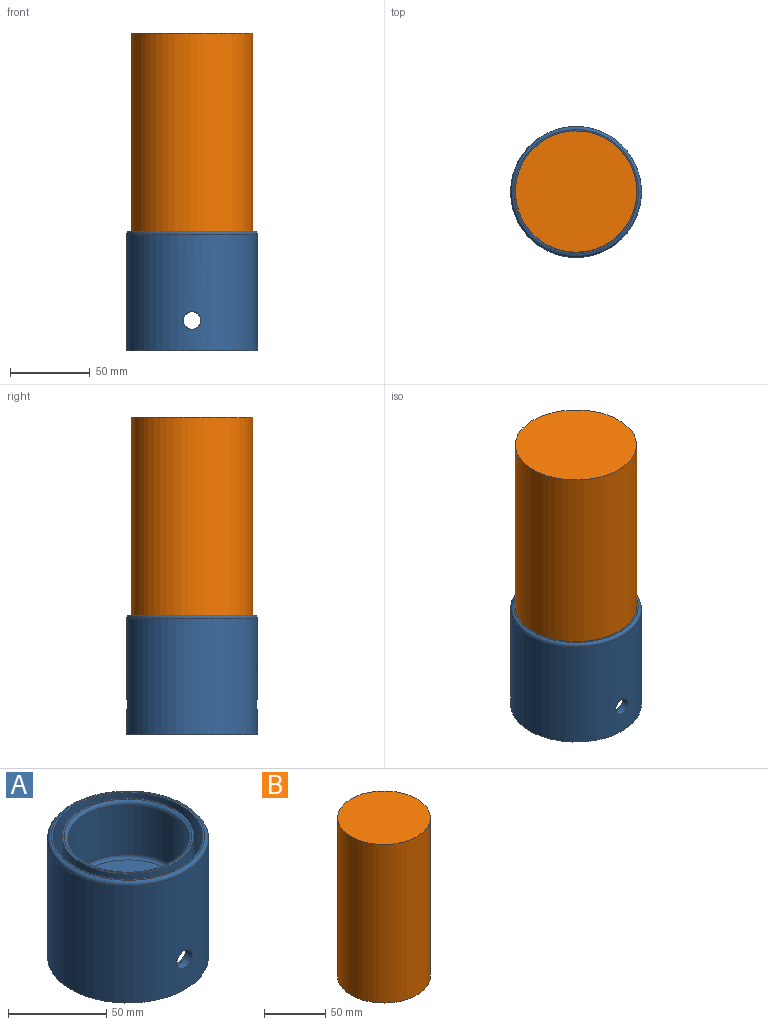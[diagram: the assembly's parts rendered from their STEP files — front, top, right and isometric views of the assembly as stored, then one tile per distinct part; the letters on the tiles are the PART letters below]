
ASSEMBLY  parts=2 mates=1
PART A: 24 faces, bbox 88.8x88.8x75 mm
  f0: cylinder r=41mm len=82mm, axis (0,0,-1), area 18615.5mm2, adj f5,f6,f22,f23
  f1: cylinder r=36.5mm len=73mm, axis (0,0,-1), area 4855.3mm2, adj f10,f11,f22,f23
  f2: plane 76x76mm, normal (0,0,1), area 1010.8mm2, adj f3,f20
  f3: cylinder r=38mm len=76mm, axis (0,0,-1), area 8356.6mm2, adj f2,f4
  f4: plane 78x78mm, normal (0,0,1), area 241.9mm2, adj f3,f5
  f5: torus R=39mm, axis (0,0,-1), area 795mm2, adj f0,f4
  f6: plane 82x82mm, normal (0,0,-1), area 1321.8mm2, adj f0,f7
  f7: cylinder r=35.5mm len=71mm, axis (0,0,-1), area 669.2mm2, adj f6,f8
  f8: plane 71x71mm, normal (0,0,-1), area 1036.7mm2, adj f7,f9
  f9: cylinder r=30.5mm len=61mm, axis (0,0,-1), area 958.2mm2, adj f8,f10
  f10: plane 73x73mm, normal (0,0,1), area 1262.9mm2, adj f1,f9
  f11: plane 73x73mm, normal (0,0,-1), area 1262.9mm2, adj f1,f12
  f12: cylinder r=30.5mm len=61mm, axis (0,0,-1), area 574.9mm2, adj f11,f13
  f13: torus R=28.5mm, axis (0,0,-1), area 587.7mm2, adj f12,f14
  f14: plane 57x57mm, normal (0,0,-1), area 1747.5mm2, adj f13,f21
  f15: plane 57x57mm, normal (0,0,1), area 1747.5mm2, adj f16,f21
  f16: torus R=28.5mm, axis (0,0,-1), area 587.7mm2, adj f15,f17
  f17: cylinder r=30.5mm len=61mm, axis (0,0,-1), area 5940.8mm2, adj f16,f18
  f18: torus R=32.5mm, axis (0,0,-1), area 616.4mm2, adj f17,f19
  f19: plane 67x67mm, normal (0,0,1), area 207.3mm2, adj f18,f20
  f20: cylinder r=33.5mm len=67mm, axis (0,0,-1), area 7367mm2, adj f2,f19
  f21: cylinder r=16mm len=32mm, axis (0,0,-1), area 502.7mm2, adj f14,f15
  f22: cylinder r=5.5mm len=11mm, axis (0,-1,0), area 156.3mm2, adj f0,f1
  f23: cylinder r=5.5mm len=11mm, axis (0,1,0), area 156.3mm2, adj f0,f1
PART B: 5 faces, bbox 76x76x159 mm
  f0: cylinder r=35mm len=155mm, axis (0,0,-1), area 34086.3mm2, adj f2,f3
  f1: cylinder r=38mm len=159mm, axis (0,0,-1), area 37963mm2, adj f2,f4
  f2: plane 76x76mm, normal (0,0,-1), area 688mm2, adj f0,f1
  f3: plane 70x70mm, normal (0,0,-1), area 3848.5mm2, adj f0
  f4: plane 76x76mm, normal (0,0,1), area 4536.5mm2, adj f1
PLACE A t=(-39.25,29.14,-155.56)mm
PLACE B t=(-39.25,29.14,-38.06)mm
MATE fastened B.f0 <-> A.f0  axis (0,0,-1) through (-39.25,29.14,-115.56)mm
